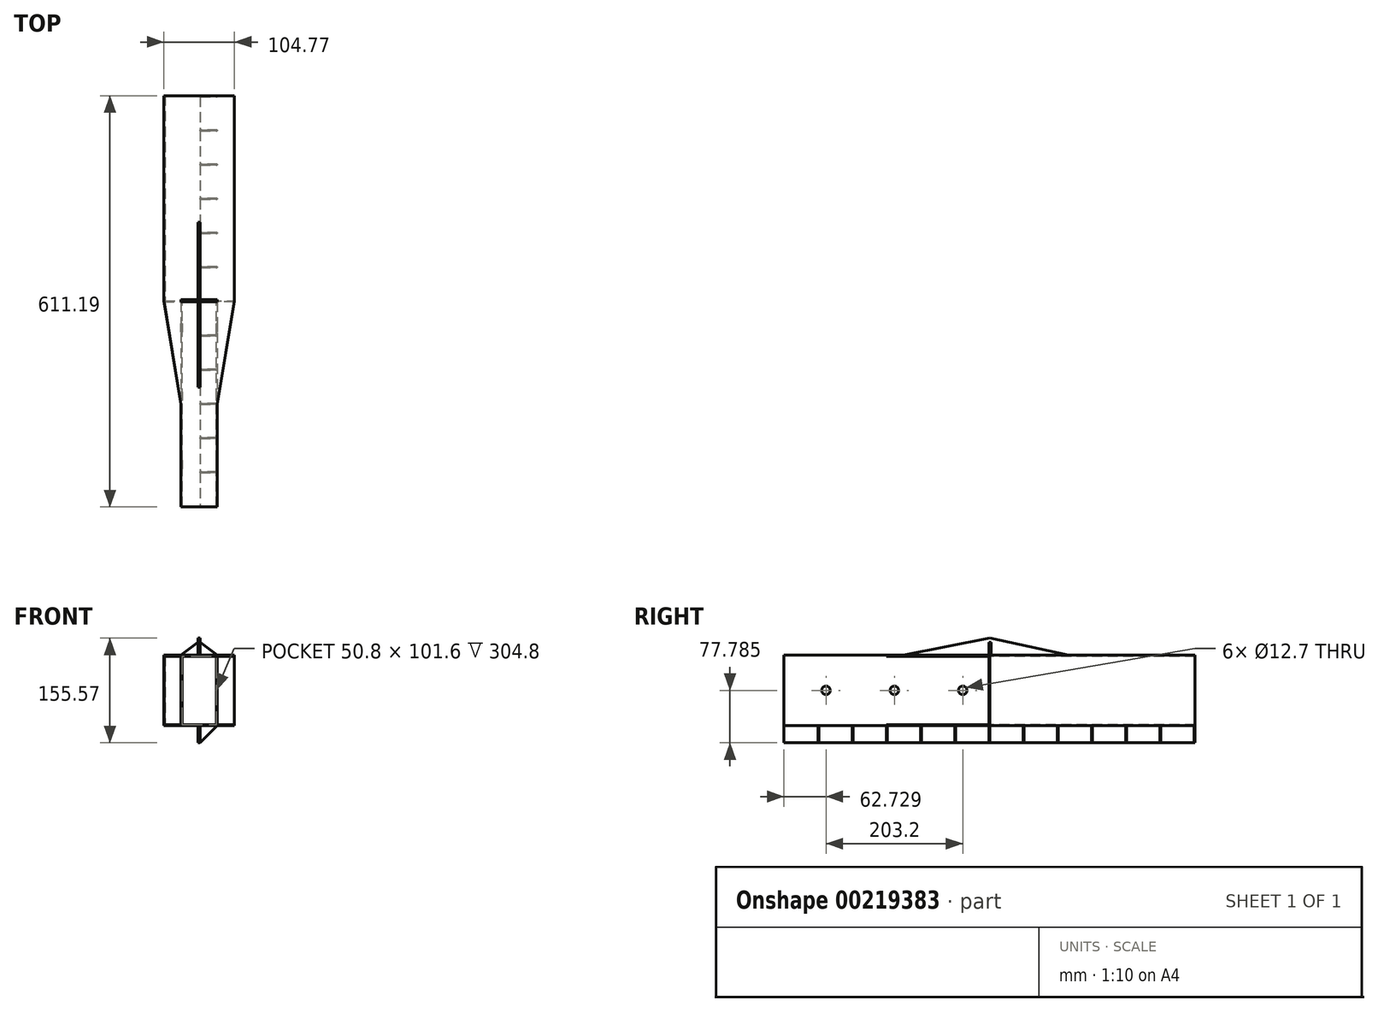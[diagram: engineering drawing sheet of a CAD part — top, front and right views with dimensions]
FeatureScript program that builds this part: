
annotation { "Feature Type Name" : "Feature", "Feature Type Description" : "" }
export const myFeature = defineFeature(function(context is Context, id is Id, definition is map)
    precondition{}
    {
        {
            var Q0;
            Q0=qCreatedBy(makeId("Front.planeOp"),FACE);
            var sketch = newSketch(context, id + "F0", { "sketchPlane" : qUnion([Q0])});
            skLineSegment(sketch, "E0.bottom", {"start": v(46.68, -42.62) * mm, "end": v(-54.92, -42.62) * mm});
            skLineSegment(sketch, "E0.top", {"start": v(46.68, 58.98) * mm, "end": v(-54.92, 58.98) * mm});
            skLineSegment(sketch, "E0.left", {"start": v(46.68, -42.62) * mm, "end": v(46.68, 58.98) * mm});
            skLineSegment(sketch, "E0.right", {"start": v(-54.92, -42.62) * mm, "end": v(-54.92, 58.98) * mm});
            skLineSegment(sketch, "E1.0", {"start": v(48.27, -44.21) * mm, "end": v(48.27, 60.56) * mm});
            skLineSegment(sketch, "E1.1", {"start": v(48.27, -44.21) * mm, "end": v(-56.5, -44.21) * mm});
            skLineSegment(sketch, "E1.2", {"start": v(-56.5, -44.21) * mm, "end": v(-56.5, 60.56) * mm});
            skLineSegment(sketch, "E1.3", {"start": v(48.27, 60.56) * mm, "end": v(-56.5, 60.56) * mm});
            skSolve(sketch);
        }
        {
            var Q0;
            Q0=makeQuery(id+"F0.imprint","IMPRINT",FACE,{"disambiguationData":[TD([[makeQuery(id+"F0.imprint","IMPRINT",EDGE,{"derivedFrom":sQuery(id+"F0.wireOp",EDGE,"E0.bottom")}),-1.0]])]});
            var Q1;
            Q1=makeQuery(id+"F0.imprint","IMPRINT",FACE,{"disambiguationData":[TD([[makeQuery(id+"F0.imprint","IMPRINT",EDGE,{"derivedFrom":sQuery(id+"F0.wireOp",EDGE,"E0.bottom")}),1.0]])]});
            extrude(context, id + "F1", {"entities" : qUnion([Q0, Q1]), "depth" : 1.59 * mm});
        }
        {
            var Q0;
            Q0=makeQuery(id+"F1.opExtrude","CAP_FACE",FACE,{"disambiguationData":[OSD([sQuery(id+"F0.wireOp",EDGE,"E1.0"),sQuery(id+"F0.wireOp",EDGE,"E1.1"),sQuery(id+"F0.wireOp",EDGE,"E1.2"),sQuery(id+"F0.wireOp",EDGE,"E1.3")])],"isStart":true});
            var sketch = newSketch(context, id + "F2", { "sketchPlane" : qUnion([Q0])});
            skLineSegment(sketch, "E2", {"start": v(-48.27, 60.56) * mm, "end": v(56.5, -44.21) * mm});
            skLineSegment(sketch, "E3.bottom", {"start": v(54.92, 58.98) * mm, "end": v(-46.68, 58.98) * mm});
            skLineSegment(sketch, "E3.top", {"start": v(54.92, -42.62) * mm, "end": v(-46.68, -42.62) * mm});
            skLineSegment(sketch, "E3.left", {"start": v(54.92, 58.98) * mm, "end": v(54.92, -42.62) * mm});
            skLineSegment(sketch, "E3.right", {"start": v(-46.68, 58.98) * mm, "end": v(-46.68, -42.62) * mm});
            skPoint(sketch, "E3.middle", {"position": v(4.12, 8.18) * mm});
            skSolve(sketch);
        }
        {
            var Q0;
            {var subQ1=sQuery(id+"F2.wireOp",EDGE,"E3.top");Q0=makeQuery(id+"F2.imprint","IMPRINT",FACE,{"disambiguationData":[TD([[makeQuery(id+"F2.imprint","IMPRINT",EDGE,{"derivedFrom":subQ1}),1.0]])]});}
            var Q1;
            {var subQ1=sQuery(id+"F2.wireOp",EDGE,"E3.bottom");Q1=makeQuery(id+"F2.imprint","IMPRINT",FACE,{"disambiguationData":[TD([[makeQuery(id+"F2.imprint","IMPRINT",EDGE,{"derivedFrom":subQ1}),-1.0]])]});}
            extrude(context, id + "F3", {"entities" : qUnion([Q0, Q1]), "operationType" : NewBodyOperationType.ADD, "depth" : 304.8 * mm});
        }
        {
            var Q0;
            Q0=makeQuery(id+"F1.opExtrude","CAP_FACE",FACE,{"disambiguationData":[OSD([sQuery(id+"F0.wireOp",EDGE,"E1.0"),sQuery(id+"F0.wireOp",EDGE,"E1.1"),sQuery(id+"F0.wireOp",EDGE,"E1.2"),sQuery(id+"F0.wireOp",EDGE,"E1.3")])],"isStart":false});
            var sketch = newSketch(context, id + "F4", { "sketchPlane" : qUnion([Q0])});
            skLineSegment(sketch, "E4", {"start": v(-56.5, 60.56) * mm, "end": v(48.27, -44.21) * mm});
            skLineSegment(sketch, "E5.bottom", {"start": v(21.28, -42.62) * mm, "end": v(-29.52, -42.62) * mm});
            skLineSegment(sketch, "E5.top", {"start": v(21.28, 58.98) * mm, "end": v(-29.52, 58.98) * mm});
            skLineSegment(sketch, "E5.left", {"start": v(21.28, -42.62) * mm, "end": v(21.28, 58.98) * mm});
            skLineSegment(sketch, "E5.right", {"start": v(-29.52, -42.62) * mm, "end": v(-29.52, 58.98) * mm});
            skPoint(sketch, "E5.middle", {"position": v(-4.12, 8.18) * mm});
            skLineSegment(sketch, "E6.0", {"start": v(22.87, 60.56) * mm, "end": v(-31.1, 60.56) * mm});
            skLineSegment(sketch, "E6.1", {"start": v(22.87, -44.21) * mm, "end": v(22.87, 60.56) * mm});
            skLineSegment(sketch, "E6.2", {"start": v(22.87, -44.21) * mm, "end": v(-31.1, -44.21) * mm});
            skLineSegment(sketch, "E6.3", {"start": v(-31.1, -44.21) * mm, "end": v(-31.1, 60.56) * mm});
            skSolve(sketch);
        }
        {
            var Q0;
            {var subQ1=sQuery(id+"F4.wireOp",EDGE,"E5.top");Q0=makeQuery(id+"F4.imprint","IMPRINT",FACE,{"disambiguationData":[TD([[makeQuery(id+"F4.imprint","IMPRINT",EDGE,{"derivedFrom":subQ1}),-1.0]])]});}
            var Q1;
            {var subQ1=sQuery(id+"F4.wireOp",EDGE,"E5.bottom");Q1=makeQuery(id+"F4.imprint","IMPRINT",FACE,{"disambiguationData":[TD([[makeQuery(id+"F4.imprint","IMPRINT",EDGE,{"derivedFrom":subQ1}),1.0]])]});}
            extrude(context, id + "F5", {"entities" : qUnion([Q0, Q1]), "operationType" : NewBodyOperationType.ADD, "depth" : 304.8 * mm});
        }
        {
            var Q0;
            Q0=makeQuery(id+"F5.opExtrude","SWEPT_FACE",FACE,{"disambiguationData":[OSD([sQuery(id+"F4.wireOp",EDGE,"E6.3")])]});
            var sketch = newSketch(context, id + "F6", { "sketchPlane" : qUnion([Q0])});
            skLineSegment(sketch, "E7", {"start": v(1.59, 58.98) * mm, "end": v(153.99, 58.98) * mm});
            skLineSegment(sketch, "E8", {"start": v(153.99, 58.98) * mm, "end": v(153.99, 60.56) * mm});
            skLineSegment(sketch, "E9", {"start": v(1.59, 8.18) * mm, "end": v(191.73, 8.18) * mm, "construction": true});
            skLineSegment(sketch, "E10.MirrorCS", {"start": v(1.59, -42.62) * mm, "end": v(153.99, -42.62) * mm});
            skLineSegment(sketch, "E11.MirrorCS", {"start": v(153.99, -42.62) * mm, "end": v(153.99, -44.21) * mm});
            skSolve(sketch);
        }
        {
            var Q0;
            {var subQ0=sQuery(id+"F6.wireOp",EDGE,"E7");Q0=makeQuery(id+"F6.imprint","IMPRINT",FACE,{"disambiguationData":[TD([[makeQuery(id+"F6.imprint","IMPRINT",EDGE,{"derivedFrom":subQ0}),1.0]])]});}
            var Q1;
            {var subQ0=sQuery(id+"F6.wireOp",EDGE,"E10.MirrorCS");Q1=makeQuery(id+"F6.imprint","IMPRINT",FACE,{"disambiguationData":[TD([[makeQuery(id+"F6.imprint","IMPRINT",EDGE,{"derivedFrom":subQ0}),-1.0]])]});}
            extrude(context, id + "F7", {"entities" : qUnion([Q0, Q1]), "operationType" : NewBodyOperationType.ADD, "depth" : 25.4 * mm});
        }
        {
            var Q0;
            Q0=makeQuery(id+"F5.opExtrude","SWEPT_FACE",FACE,{"disambiguationData":[OSD([sQuery(id+"F4.wireOp",EDGE,"E6.1")])]});
            var sketch = newSketch(context, id + "F8", { "sketchPlane" : qUnion([Q0])});
            skLineSegment(sketch, "E12", {"start": v(-1.59, 58.98) * mm, "end": v(-153.99, 58.98) * mm});
            skLineSegment(sketch, "E13", {"start": v(-153.99, 58.98) * mm, "end": v(-153.99, 60.56) * mm});
            skLineSegment(sketch, "E14", {"start": v(0, 8.18) * mm, "end": v(-173.63, 8.18) * mm, "construction": true});
            skPoint(sketch, "E14.startSnap0", {"position": v(-1.59, 8.18) * mm});
            skLineSegment(sketch, "E15.MirrorCS", {"start": v(-1.59, -42.62) * mm, "end": v(-153.99, -42.62) * mm});
            skLineSegment(sketch, "E16.MirrorCS", {"start": v(-153.99, -42.62) * mm, "end": v(-153.99, -44.21) * mm});
            skSolve(sketch);
        }
        {
            var Q0;
            {var subQ0=sQuery(id+"F8.wireOp",EDGE,"E12");Q0=makeQuery(id+"F8.imprint","IMPRINT",FACE,{"disambiguationData":[TD([[makeQuery(id+"F8.imprint","IMPRINT",EDGE,{"derivedFrom":subQ0}),-1.0]])]});}
            var Q1;
            {var subQ0=sQuery(id+"F8.wireOp",EDGE,"E15.MirrorCS");Q1=makeQuery(id+"F8.imprint","IMPRINT",FACE,{"disambiguationData":[TD([[makeQuery(id+"F8.imprint","IMPRINT",EDGE,{"derivedFrom":subQ0}),1.0]])]});}
            extrude(context, id + "F9", {"entities" : qUnion([Q0, Q1]), "operationType" : NewBodyOperationType.ADD, "depth" : 25.4 * mm});
        }
        {
            var Q0;
            {var subQ0=sQuery(id+"F4.wireOp",EDGE,"E6.0");var subQ1=sQuery(id+"F0.wireOp",EDGE,"E1.3");Q0=makeQuery(id+"F9.boolean.opBoolean","MERGE",FACE,{"derivedFrom":[makeQuery(id+"F7.boolean.opBoolean","MERGE",FACE,{"derivedFrom":[makeQuery(id+"F5.boolean.opBoolean","MERGE",FACE,{"derivedFrom":[makeQuery(id+"F3.boolean.opBoolean","MERGE",FACE,{"derivedFrom":[makeQuery(id+"F1.opExtrude","SWEPT_FACE",FACE,{"disambiguationData":[OSD([subQ1])]}),makeQuery(id+"F3.opExtrude","SWEPT_FACE",FACE,{"disambiguationData":[OSD([subQ1])]})]}),makeQuery(id+"F5.opExtrude","SWEPT_FACE",FACE,{"disambiguationData":[OSD([subQ0])]})]}),makeQuery(id+"F7.opExtrude","SWEPT_FACE",FACE,{"disambiguationData":[OSD([subQ1,subQ0,sQuery(id+"F4.wireOp",EDGE,"E6.3")])]})]}),makeQuery(id+"F9.opExtrude","SWEPT_FACE",FACE,{"disambiguationData":[OSD([subQ1,subQ0,sQuery(id+"F4.wireOp",EDGE,"E6.1")])]})]});}
            var sketch = newSketch(context, id + "F10", { "sketchPlane" : qUnion([Q0])});
            skLineSegment(sketch, "E17", {"start": v(48.27, 0) * mm, "end": v(22.87, -153.99) * mm});
            skLineSegment(sketch, "E18", {"start": v(-56.5, 0) * mm, "end": v(-31.1, -153.99) * mm});
            skSolve(sketch);
        }
        {
            var Q0;
            Q0 = qSketchRegion(id + "F10", true);
            var Q1;
            {var subQ0=sQuery(id+"F10.wireOp",EDGE,"E18");Q1=makeQuery(id+"F10.imprint","IMPRINT",FACE,{"disambiguationData":[TD([[makeQuery(id+"F10.imprint","IMPRINT",EDGE,{"derivedFrom":subQ0}),-1.0]])]});}
            var Q2;
            {var subQ0=sQuery(id+"F10.wireOp",EDGE,"E17");Q2=makeQuery(id+"F10.imprint","IMPRINT",FACE,{"disambiguationData":[TD([[makeQuery(id+"F10.imprint","IMPRINT",EDGE,{"derivedFrom":subQ0}),1.0]])]});}
            extrude(context, id + "F11", {"entities" : qUnion([Q0, Q1, Q2]), "operationType" : NewBodyOperationType.REMOVE, "oppositeDirection" : true, "depth" : 177.8 * mm});
        }
        {
            var Q0;
            {var subQ0=sQuery(id+"F4.wireOp",EDGE,"E6.2");var subQ1=sQuery(id+"F0.wireOp",EDGE,"E1.1");Q0=makeQuery(id+"F9.boolean.opBoolean","MERGE",FACE,{"derivedFrom":[makeQuery(id+"F7.boolean.opBoolean","MERGE",FACE,{"derivedFrom":[makeQuery(id+"F5.boolean.opBoolean","MERGE",FACE,{"derivedFrom":[makeQuery(id+"F3.boolean.opBoolean","MERGE",FACE,{"derivedFrom":[makeQuery(id+"F1.opExtrude","SWEPT_FACE",FACE,{"disambiguationData":[OSD([subQ1])]}),makeQuery(id+"F3.opExtrude","SWEPT_FACE",FACE,{"disambiguationData":[OSD([subQ1])]})]}),makeQuery(id+"F5.opExtrude","SWEPT_FACE",FACE,{"disambiguationData":[OSD([subQ0])]})]}),makeQuery(id+"F7.opExtrude","SWEPT_FACE",FACE,{"disambiguationData":[OSD([subQ1,subQ0,sQuery(id+"F4.wireOp",EDGE,"E6.3")])]})]}),makeQuery(id+"F9.opExtrude","SWEPT_FACE",FACE,{"disambiguationData":[OSD([subQ1,sQuery(id+"F4.wireOp",EDGE,"E6.1"),subQ0])]})]});}
            var sketch = newSketch(context, id + "F12", { "sketchPlane" : qUnion([Q0])});
            skLineSegment(sketch, "E19", {"start": v(-4.12, -304.8) * mm, "end": v(-4.12, 306.39) * mm, "construction": true});
            skLineSegment(sketch, "E20", {"start": v(-5.7, -304.8) * mm, "end": v(-5.7, 306.39) * mm});
            skLineSegment(sketch, "E21.MirrorCS", {"start": v(-2.53, -304.8) * mm, "end": v(-2.53, 306.39) * mm});
            skSolve(sketch);
        }
        {
            var Q0;
            {var subQ0=sQuery(id+"F12.wireOp",EDGE,"E20");Q0=makeQuery(id+"F12.imprint","IMPRINT",FACE,{"disambiguationData":[TD([[makeQuery(id+"F12.imprint","IMPRINT",EDGE,{"derivedFrom":subQ0}),-1.0]])]});}
            extrude(context, id + "F13", {"entities" : qUnion([Q0]), "operationType" : NewBodyOperationType.ADD, "depth" : 25.4 * mm});
        }
        {
            var Q0;
            Q0=makeQuery(id+"F5.opExtrude","SWEPT_FACE",FACE,{"disambiguationData":[OSD([sQuery(id+"F4.wireOp",EDGE,"E6.3")])]});
            var sketch = newSketch(context, id + "F14", { "sketchPlane" : qUnion([Q0])});
            skLineSegment(sketch, "E22", {"start": v(1.59, 8.18) * mm, "end": v(306.39, 8.18) * mm, "construction": true});
            skCircle(sketch, "E23", {"center": v(40.46, 8.18) * mm, "radius": 6.35 * mm});
            skCircle(sketch, "E24", {"center": v(142.06, 8.18) * mm, "radius": 6.35 * mm});
            skCircle(sketch, "E25", {"center": v(243.66, 8.18) * mm, "radius": 6.35 * mm});
            skSolve(sketch);
        }
        {
            var Q0;
            Q0=makeQuery(id+"F14.imprint","IMPRINT",FACE,{"disambiguationData":[TD([[makeQuery(id+"F14.imprint","IMPRINT",EDGE,{"derivedFrom":sQuery(id+"F14.wireOp",EDGE,"E23")}),1.0]])]});
            var Q1;
            Q1=makeQuery(id+"F14.imprint","IMPRINT",FACE,{"disambiguationData":[TD([[makeQuery(id+"F14.imprint","IMPRINT",EDGE,{"derivedFrom":sQuery(id+"F14.wireOp",EDGE,"E24")}),1.0]])]});
            var Q2;
            Q2=makeQuery(id+"F14.imprint","IMPRINT",FACE,{"disambiguationData":[TD([[makeQuery(id+"F14.imprint","IMPRINT",EDGE,{"derivedFrom":sQuery(id+"F14.wireOp",EDGE,"E25")}),1.0]])]});
            extrude(context, id + "F15", {"entities" : qUnion([Q0, Q1, Q2]), "operationType" : NewBodyOperationType.REMOVE, "oppositeDirection" : true, "depth" : 213.36 * mm});
        }
        {
            var Q0;
            {var subQ0=sQuery(id+"F0.wireOp",EDGE,"E1.1");var subQ1=sQuery(id+"F4.wireOp",EDGE,"E6.3");var subQ2=sQuery(id+"F4.wireOp",EDGE,"E6.2");var subQ3=sQuery(id+"F4.wireOp",EDGE,"E6.1");var subQ6=sQuery(id+"F0.wireOp",EDGE,"E1.0");Q0=makeQuery(id+"F13.boolean.opBoolean","SPLIT",FACE,{"disambiguationData":[TD([makeQuery(id+"F1.opExtrude","SWEPT_FACE",FACE,{"disambiguationData":[OSD([subQ6])]})])],"derivedFrom":makeQuery(id+"F9.boolean.opBoolean","MERGE",FACE,{"derivedFrom":[makeQuery(id+"F7.boolean.opBoolean","MERGE",FACE,{"derivedFrom":[makeQuery(id+"F5.boolean.opBoolean","MERGE",FACE,{"derivedFrom":[makeQuery(id+"F3.boolean.opBoolean","MERGE",FACE,{"derivedFrom":[makeQuery(id+"F1.opExtrude","SWEPT_FACE",FACE,{"disambiguationData":[OSD([subQ0])]}),makeQuery(id+"F3.opExtrude","SWEPT_FACE",FACE,{"disambiguationData":[OSD([subQ0])]})]}),makeQuery(id+"F5.opExtrude","SWEPT_FACE",FACE,{"disambiguationData":[OSD([subQ2])]})]}),makeQuery(id+"F7.opExtrude","SWEPT_FACE",FACE,{"disambiguationData":[OSD([subQ0,subQ2,subQ1])]})]}),makeQuery(id+"F9.opExtrude","SWEPT_FACE",FACE,{"disambiguationData":[OSD([subQ0,subQ3,subQ2])]})]})});}
            var sketch = newSketch(context, id + "F16", { "sketchPlane" : qUnion([Q0])});
            skLineSegment(sketch, "E26", {"start": v(-2.53, -304.8) * mm, "end": v(22.87, -304.8) * mm});
            skLineSegment(sketch, "E27", {"start": v(22.87, -304.8) * mm, "end": v(22.87, -303.21) * mm});
            skLineSegment(sketch, "E28", {"start": v(22.87, -303.21) * mm, "end": v(-2.53, -303.21) * mm});
            skLineSegment(sketch, "E29.0.1.0", {"start": v(22.87, -252.41) * mm, "end": v(-2.53, -252.41) * mm});
            skLineSegment(sketch, "E29.0.1.1", {"start": v(22.87, -254) * mm, "end": v(22.87, -252.41) * mm});
            skLineSegment(sketch, "E29.0.1.2", {"start": v(-2.53, -254) * mm, "end": v(22.87, -254) * mm});
            skLineSegment(sketch, "E29.0.2.0", {"start": v(22.87, -201.61) * mm, "end": v(-2.53, -201.61) * mm});
            skLineSegment(sketch, "E29.0.2.1", {"start": v(22.87, -203.2) * mm, "end": v(22.87, -201.61) * mm});
            skLineSegment(sketch, "E29.0.2.2", {"start": v(-2.53, -203.2) * mm, "end": v(22.87, -203.2) * mm});
            skLineSegment(sketch, "E29.0.3.0", {"start": v(22.87, -150.81) * mm, "end": v(-2.53, -150.81) * mm});
            skLineSegment(sketch, "E29.0.3.1", {"start": v(22.87, -152.4) * mm, "end": v(22.87, -150.81) * mm});
            skLineSegment(sketch, "E29.0.3.2", {"start": v(-2.53, -152.4) * mm, "end": v(22.87, -152.4) * mm});
            skLineSegment(sketch, "E29.0.4.0", {"start": v(22.87, -100.01) * mm, "end": v(-2.53, -100.01) * mm});
            skLineSegment(sketch, "E29.0.4.1", {"start": v(22.87, -101.6) * mm, "end": v(22.87, -100.01) * mm});
            skLineSegment(sketch, "E29.0.4.2", {"start": v(-2.53, -101.6) * mm, "end": v(22.87, -101.6) * mm});
            skLineSegment(sketch, "E29.0.5.0", {"start": v(22.87, -49.21) * mm, "end": v(-2.53, -49.21) * mm});
            skLineSegment(sketch, "E29.0.5.1", {"start": v(22.87, -50.8) * mm, "end": v(22.87, -49.21) * mm});
            skLineSegment(sketch, "E29.0.5.2", {"start": v(-2.53, -50.8) * mm, "end": v(22.87, -50.8) * mm});
            skLineSegment(sketch, "E29.0.6.0", {"start": v(22.87, 1.59) * mm, "end": v(-2.53, 1.59) * mm});
            skLineSegment(sketch, "E29.0.6.1", {"start": v(22.87, 0) * mm, "end": v(22.87, 1.59) * mm});
            skLineSegment(sketch, "E29.0.6.2", {"start": v(-2.53, 0) * mm, "end": v(22.87, 0) * mm});
            skLineSegment(sketch, "E29.0.7.0", {"start": v(22.87, 52.39) * mm, "end": v(-2.53, 52.39) * mm});
            skLineSegment(sketch, "E29.0.7.1", {"start": v(22.87, 50.8) * mm, "end": v(22.87, 52.39) * mm});
            skLineSegment(sketch, "E29.0.7.2", {"start": v(-2.53, 50.8) * mm, "end": v(22.87, 50.8) * mm});
            skLineSegment(sketch, "E29.0.8.0", {"start": v(22.87, 103.19) * mm, "end": v(-2.53, 103.19) * mm});
            skLineSegment(sketch, "E29.0.8.1", {"start": v(22.87, 101.6) * mm, "end": v(22.87, 103.19) * mm});
            skLineSegment(sketch, "E29.0.8.2", {"start": v(-2.53, 101.6) * mm, "end": v(22.87, 101.6) * mm});
            skLineSegment(sketch, "E29.0.9.0", {"start": v(22.87, 153.99) * mm, "end": v(-2.53, 153.99) * mm});
            skLineSegment(sketch, "E29.0.9.1", {"start": v(22.87, 152.4) * mm, "end": v(22.87, 153.99) * mm});
            skLineSegment(sketch, "E29.0.9.2", {"start": v(-2.53, 152.4) * mm, "end": v(22.87, 152.4) * mm});
            skLineSegment(sketch, "E29.0.10.0", {"start": v(22.87, 204.79) * mm, "end": v(-2.53, 204.79) * mm});
            skLineSegment(sketch, "E29.0.10.1", {"start": v(22.87, 203.2) * mm, "end": v(22.87, 204.79) * mm});
            skLineSegment(sketch, "E29.0.10.2", {"start": v(-2.53, 203.2) * mm, "end": v(22.87, 203.2) * mm});
            skLineSegment(sketch, "E29.0.11.0", {"start": v(22.87, 255.59) * mm, "end": v(-2.53, 255.59) * mm});
            skLineSegment(sketch, "E29.0.11.1", {"start": v(22.87, 254) * mm, "end": v(22.87, 255.59) * mm});
            skLineSegment(sketch, "E29.0.11.2", {"start": v(-2.53, 254) * mm, "end": v(22.87, 254) * mm});
            skLineSegment(sketch, "E29.direction1", {"start": v(-2.53, -303.21) * mm, "end": v(22.87, -303.21) * mm, "construction": true});
            skLineSegment(sketch, "E29.direction2", {"start": v(-2.53, -303.21) * mm, "end": v(-2.53, -252.41) * mm, "construction": true});
            skSolve(sketch);
        }
        {
            var Q0;
            Q0 = qSketchRegion(id + "F16", true);
            var Q1;
            {var subQ0=sQuery(id+"F16.wireOp",EDGE,"E26");Q1=makeQuery(id+"F16.imprint","IMPRINT",FACE,{"disambiguationData":[TD([[makeQuery(id+"F16.imprint","IMPRINT",EDGE,{"derivedFrom":subQ0}),-1.0]])]});}
            var Q2;
            {var subQ0=sQuery(id+"F16.wireOp",EDGE,"E29.0.1.0");Q2=makeQuery(id+"F16.imprint","IMPRINT",FACE,{"disambiguationData":[TD([[makeQuery(id+"F16.imprint","IMPRINT",EDGE,{"derivedFrom":subQ0}),1.0]])]});}
            var Q3;
            {var subQ0=sQuery(id+"F16.wireOp",EDGE,"E29.0.2.0");Q3=makeQuery(id+"F16.imprint","IMPRINT",FACE,{"disambiguationData":[TD([[makeQuery(id+"F16.imprint","IMPRINT",EDGE,{"derivedFrom":subQ0}),1.0]])]});}
            var Q4;
            {var subQ0=sQuery(id+"F16.wireOp",EDGE,"E29.0.3.0");Q4=makeQuery(id+"F16.imprint","IMPRINT",FACE,{"disambiguationData":[TD([[makeQuery(id+"F16.imprint","IMPRINT",EDGE,{"derivedFrom":subQ0}),1.0]])]});}
            var Q5;
            {var subQ0=sQuery(id+"F16.wireOp",EDGE,"E29.0.4.0");Q5=makeQuery(id+"F16.imprint","IMPRINT",FACE,{"disambiguationData":[TD([[makeQuery(id+"F16.imprint","IMPRINT",EDGE,{"derivedFrom":subQ0}),1.0]])]});}
            var Q6;
            {var subQ0=sQuery(id+"F16.wireOp",EDGE,"E29.0.5.0");Q6=makeQuery(id+"F16.imprint","IMPRINT",FACE,{"disambiguationData":[TD([[makeQuery(id+"F16.imprint","IMPRINT",EDGE,{"derivedFrom":subQ0}),1.0]])]});}
            var Q7;
            {var subQ0=sQuery(id+"F16.wireOp",EDGE,"E29.0.6.0");Q7=makeQuery(id+"F16.imprint","IMPRINT",FACE,{"disambiguationData":[TD([[makeQuery(id+"F16.imprint","IMPRINT",EDGE,{"derivedFrom":subQ0}),1.0]])]});}
            var Q8;
            {var subQ0=sQuery(id+"F16.wireOp",EDGE,"E29.0.8.0");Q8=makeQuery(id+"F16.imprint","IMPRINT",FACE,{"disambiguationData":[TD([[makeQuery(id+"F16.imprint","IMPRINT",EDGE,{"derivedFrom":subQ0}),1.0]])]});}
            var Q9;
            {var subQ0=sQuery(id+"F16.wireOp",EDGE,"E29.0.7.0");Q9=makeQuery(id+"F16.imprint","IMPRINT",FACE,{"disambiguationData":[TD([[makeQuery(id+"F16.imprint","IMPRINT",EDGE,{"derivedFrom":subQ0}),1.0]])]});}
            var Q10;
            {var subQ0=sQuery(id+"F16.wireOp",EDGE,"E29.0.9.0");Q10=makeQuery(id+"F16.imprint","IMPRINT",FACE,{"disambiguationData":[TD([[makeQuery(id+"F16.imprint","IMPRINT",EDGE,{"derivedFrom":subQ0}),1.0]])]});}
            var Q11;
            {var subQ0=sQuery(id+"F16.wireOp",EDGE,"E29.0.10.0");Q11=makeQuery(id+"F16.imprint","IMPRINT",FACE,{"disambiguationData":[TD([[makeQuery(id+"F16.imprint","IMPRINT",EDGE,{"derivedFrom":subQ0}),1.0]])]});}
            var Q12;
            {var subQ0=sQuery(id+"F16.wireOp",EDGE,"E29.0.11.0");Q12=makeQuery(id+"F16.imprint","IMPRINT",FACE,{"disambiguationData":[TD([[makeQuery(id+"F16.imprint","IMPRINT",EDGE,{"derivedFrom":subQ0}),1.0]])]});}
            extrude(context, id + "F17", {"entities" : qUnion([Q0, Q1, Q2, Q3, Q4, Q5, Q6, Q7, Q8, Q9, Q10, Q11, Q12]), "operationType" : NewBodyOperationType.ADD, "depth" : 25.4 * mm});
        }
        {
            var Q0;
            {var subQ0=sQuery(id+"F0.wireOp",EDGE,"E1.1");Q0=makeQuery(id+"F17.boolean.opBoolean","MERGE",FACE,{"derivedFrom":[makeQuery(id+"F13.boolean.opBoolean","MERGE",FACE,{"derivedFrom":[makeQuery(id+"F3.opExtrude","CAP_FACE",FACE,{"disambiguationData":[OSD([sQuery(id+"F0.wireOp",EDGE,"E1.0"),subQ0,sQuery(id+"F0.wireOp",EDGE,"E1.2"),sQuery(id+"F0.wireOp",EDGE,"E1.3"),sQuery(id+"F2.wireOp",EDGE,"E3.bottom"),sQuery(id+"F2.wireOp",EDGE,"E3.top"),sQuery(id+"F2.wireOp",EDGE,"E3.left"),sQuery(id+"F2.wireOp",EDGE,"E3.right")])],"isStart":false}),makeQuery(id+"F13.opExtrude","SWEPT_FACE",FACE,{"disambiguationData":[OSD([subQ0])]})]}),makeQuery(id+"F17.opExtrude","SWEPT_FACE",FACE,{"disambiguationData":[OSD([sQuery(id+"F16.wireOp",EDGE,"E26")])]})]});}
            var sketch = newSketch(context, id + "F18", { "sketchPlane" : qUnion([Q0])});
            skLineSegment(sketch, "E30", {"start": v(2.35, -69.61) * mm, "end": v(-22.87, -44.21) * mm});
            skSolve(sketch);
        }
        {
            var Q0;
            Q0 = qSketchRegion(id + "F18", true);
            var Q1;
            {var subQ0=sQuery(id+"F18.wireOp",EDGE,"E30");Q1=makeQuery(id+"F18.imprint","IMPRINT",FACE,{"disambiguationData":[TD([[makeQuery(id+"F18.imprint","IMPRINT",EDGE,{"derivedFrom":subQ0}),1.0]])]});}
            extrude(context, id + "F19", {"entities" : qUnion([Q0, Q1]), "operationType" : NewBodyOperationType.REMOVE, "oppositeDirection" : true, "depth" : 1828.8 * mm});
        }
        {
            var Q0;
            {var subQ0=sQuery(id+"F4.wireOp",EDGE,"E6.0");var subQ1=sQuery(id+"F0.wireOp",EDGE,"E1.3");Q0=makeQuery(id+"F9.boolean.opBoolean","MERGE",FACE,{"derivedFrom":[makeQuery(id+"F7.boolean.opBoolean","MERGE",FACE,{"derivedFrom":[makeQuery(id+"F5.boolean.opBoolean","MERGE",FACE,{"derivedFrom":[makeQuery(id+"F3.boolean.opBoolean","MERGE",FACE,{"derivedFrom":[makeQuery(id+"F1.opExtrude","SWEPT_FACE",FACE,{"disambiguationData":[OSD([subQ1])]}),makeQuery(id+"F3.opExtrude","SWEPT_FACE",FACE,{"disambiguationData":[OSD([subQ1])]})]}),makeQuery(id+"F5.opExtrude","SWEPT_FACE",FACE,{"disambiguationData":[OSD([subQ0])]})]}),makeQuery(id+"F7.opExtrude","SWEPT_FACE",FACE,{"disambiguationData":[OSD([subQ1,subQ0,sQuery(id+"F4.wireOp",EDGE,"E6.3")])]})]}),makeQuery(id+"F9.opExtrude","SWEPT_FACE",FACE,{"disambiguationData":[OSD([subQ1,subQ0,sQuery(id+"F4.wireOp",EDGE,"E6.1")])]})]});}
            var sketch = newSketch(context, id + "F20", { "sketchPlane" : qUnion([Q0])});
            skLineSegment(sketch, "E31", {"start": v(-4.12, 304.8) * mm, "end": v(-4.12, -306.39) * mm});
            skLineSegment(sketch, "E32", {"start": v(-4.12, 116.6) * mm, "end": v(-2.53, 116.6) * mm});
            skLineSegment(sketch, "E33", {"start": v(-2.53, 116.6) * mm, "end": v(-2.53, -128.42) * mm});
            skLineSegment(sketch, "E34", {"start": v(-2.53, -128.42) * mm, "end": v(-4.12, -128.42) * mm});
            skLineSegment(sketch, "E35.MirrorCS", {"start": v(-4.12, 116.6) * mm, "end": v(-5.7, 116.6) * mm});
            skLineSegment(sketch, "E36.MirrorCS", {"start": v(-5.7, 116.6) * mm, "end": v(-5.7, -128.42) * mm});
            skLineSegment(sketch, "E37.MirrorCS", {"start": v(-5.7, -128.42) * mm, "end": v(-4.12, -128.42) * mm});
            skSolve(sketch);
        }
        {
            var Q0;
            {var subQ0=sQuery(id+"F20.wireOp",EDGE,"E35.MirrorCS");Q0=makeQuery(id+"F20.imprint","IMPRINT",FACE,{"disambiguationData":[TD([[makeQuery(id+"F20.imprint","IMPRINT",EDGE,{"derivedFrom":subQ0}),1.0]])]});}
            var Q1;
            {var subQ0=sQuery(id+"F20.wireOp",EDGE,"E32");Q1=makeQuery(id+"F20.imprint","IMPRINT",FACE,{"disambiguationData":[TD([[makeQuery(id+"F20.imprint","IMPRINT",EDGE,{"derivedFrom":subQ0}),-1.0]])]});}
            extrude(context, id + "F21", {"entities" : qUnion([Q0, Q1]), "operationType" : NewBodyOperationType.ADD, "depth" : 25.4 * mm});
        }
        {
            var Q0;
            Q0=makeQuery(id+"F21.opExtrude","SWEPT_FACE",FACE,{"disambiguationData":[OSD([sQuery(id+"F20.wireOp",EDGE,"E36.MirrorCS")])]});
            var sketch = newSketch(context, id + "F22", { "sketchPlane" : qUnion([Q0])});
            skLineSegment(sketch, "E38", {"start": v(-116.6, 60.56) * mm, "end": v(0, 85.96) * mm});
            skLineSegment(sketch, "E39", {"start": v(0, 85.96) * mm, "end": v(128.42, 60.56) * mm});
            skSolve(sketch);
        }
        {
            var Q0;
            Q0 = qSketchRegion(id + "F22", true);
            var Q1;
            {var subQ0=sQuery(id+"F22.wireOp",EDGE,"E38");Q1=makeQuery(id+"F22.imprint","IMPRINT",FACE,{"disambiguationData":[TD([[makeQuery(id+"F22.imprint","IMPRINT",EDGE,{"derivedFrom":subQ0}),1.0]])]});}
            var Q2;
            {var subQ0=sQuery(id+"F22.wireOp",EDGE,"E39");Q2=makeQuery(id+"F22.imprint","IMPRINT",FACE,{"disambiguationData":[TD([[makeQuery(id+"F22.imprint","IMPRINT",EDGE,{"derivedFrom":subQ0}),1.0]])]});}
            extrude(context, id + "F23", {"entities" : qUnion([Q0, Q1, Q2]), "operationType" : NewBodyOperationType.REMOVE, "oppositeDirection" : true, "depth" : 25.4 * mm});
        }
        {
            var Q0;
            Q0=makeQuery(id+"F21.opExtrude","SWEPT_FACE",FACE,{"disambiguationData":[OSD([sQuery(id+"F20.wireOp",EDGE,"E36.MirrorCS")])]});
            var sketch = newSketch(context, id + "F24", { "sketchPlane" : qUnion([Q0])});
            skLineSegment(sketch, "E40", {"start": v(0, 85.96) * mm, "end": v(0, 60.56) * mm});
            skLineSegment(sketch, "E41", {"start": v(-1.59, 60.56) * mm, "end": v(-1.59, 79.61) * mm});
            skLineSegment(sketch, "E42", {"start": v(-1.59, 79.61) * mm, "end": v(0, 79.61) * mm});
            skLineSegment(sketch, "E43.MirrorCS", {"start": v(1.59, 79.61) * mm, "end": v(0, 79.61) * mm});
            skLineSegment(sketch, "E44.MirrorCS", {"start": v(1.59, 60.56) * mm, "end": v(1.59, 79.61) * mm});
            skSolve(sketch);
        }
        {
            var Q0;
            {var subQ4=sQuery(id+"F24.wireOp",EDGE,"E41");Q0=makeQuery(id+"F24.imprint","IMPRINT",FACE,{"disambiguationData":[TD([[makeQuery(id+"F24.imprint","IMPRINT",EDGE,{"derivedFrom":subQ4}),-1.0]])]});}
            var Q1;
            {var subQ3=sQuery(id+"F24.wireOp",EDGE,"E43.MirrorCS");Q1=makeQuery(id+"F24.imprint","IMPRINT",FACE,{"disambiguationData":[TD([[makeQuery(id+"F24.imprint","IMPRINT",EDGE,{"derivedFrom":subQ3}),1.0]])]});}
            extrude(context, id + "F25", {"entities" : qUnion([Q0, Q1]), "operationType" : NewBodyOperationType.ADD, "depth" : 25.4 * mm, "hasSecondDirection" : true, "secondDirectionOppositeDirection" : true, "secondDirectionDepth" : 28.57 * mm});
        }
        {
            var Q0;
            {var subQ2=sQuery(id+"F20.wireOp",EDGE,"E36.MirrorCS");var subQ3=sQuery(id+"F24.wireOp",EDGE,"E44.MirrorCS");Q0=makeQuery(id+"F25.boolean.opBoolean","SPLIT",FACE,{"disambiguationData":[TD([makeQuery(id+"F21.opExtrude","SWEPT_FACE",FACE,{"disambiguationData":[OSD([subQ2])]})])],"derivedFrom":makeQuery(id+"F25.opExtrude","SWEPT_FACE",FACE,{"disambiguationData":[OSD([subQ3])]})});}
            var sketch = newSketch(context, id + "F26", { "sketchPlane" : qUnion([Q0])});
            skLineSegment(sketch, "E45", {"start": v(-5.7, 79.61) * mm, "end": v(-31.1, 60.56) * mm});
            skSolve(sketch);
        }
        {
            var Q0;
            Q0 = qSketchRegion(id + "F26", true);
            var Q1;
            Q1=makeQuery(id+"F26.imprint","IMPRINT",FACE,{"disambiguationData":[TD([[makeQuery(id+"F26.imprint","IMPRINT",EDGE,{"derivedFrom":sQuery(id+"F26.wireOp",EDGE,"E45")}),-1.0]])]});
            extrude(context, id + "F27", {"entities" : qUnion([Q0, Q1]), "operationType" : NewBodyOperationType.REMOVE, "oppositeDirection" : true, "depth" : 25.4 * mm});
        }
        {
            var Q0;
            {var subQ2=sQuery(id+"F24.wireOp",EDGE,"E44.MirrorCS");Q0=makeQuery(id+"F25.boolean.opBoolean","SPLIT",FACE,{"disambiguationData":[TD([makeQuery(id+"F21.opExtrude","SWEPT_FACE",FACE,{"disambiguationData":[OSD([sQuery(id+"F20.wireOp",EDGE,"E33")])]})])],"derivedFrom":makeQuery(id+"F25.opExtrude","SWEPT_FACE",FACE,{"disambiguationData":[OSD([subQ2])]})});}
            var sketch = newSketch(context, id + "F28", { "sketchPlane" : qUnion([Q0])});
            skLineSegment(sketch, "E46", {"start": v(-2.53, 79.61) * mm, "end": v(22.87, 60.56) * mm});
            skSolve(sketch);
        }
        {
            var Q0;
            Q0 = qSketchRegion(id + "F28", true);
            var Q1;
            Q1=makeQuery(id+"F28.imprint","IMPRINT",FACE,{"disambiguationData":[TD([[makeQuery(id+"F28.imprint","IMPRINT",EDGE,{"derivedFrom":sQuery(id+"F28.wireOp",EDGE,"E46")}),1.0]])]});
            extrude(context, id + "F29", {"entities" : qUnion([Q0, Q1]), "operationType" : NewBodyOperationType.REMOVE, "oppositeDirection" : true, "depth" : 25.4 * mm});
        }
    });
